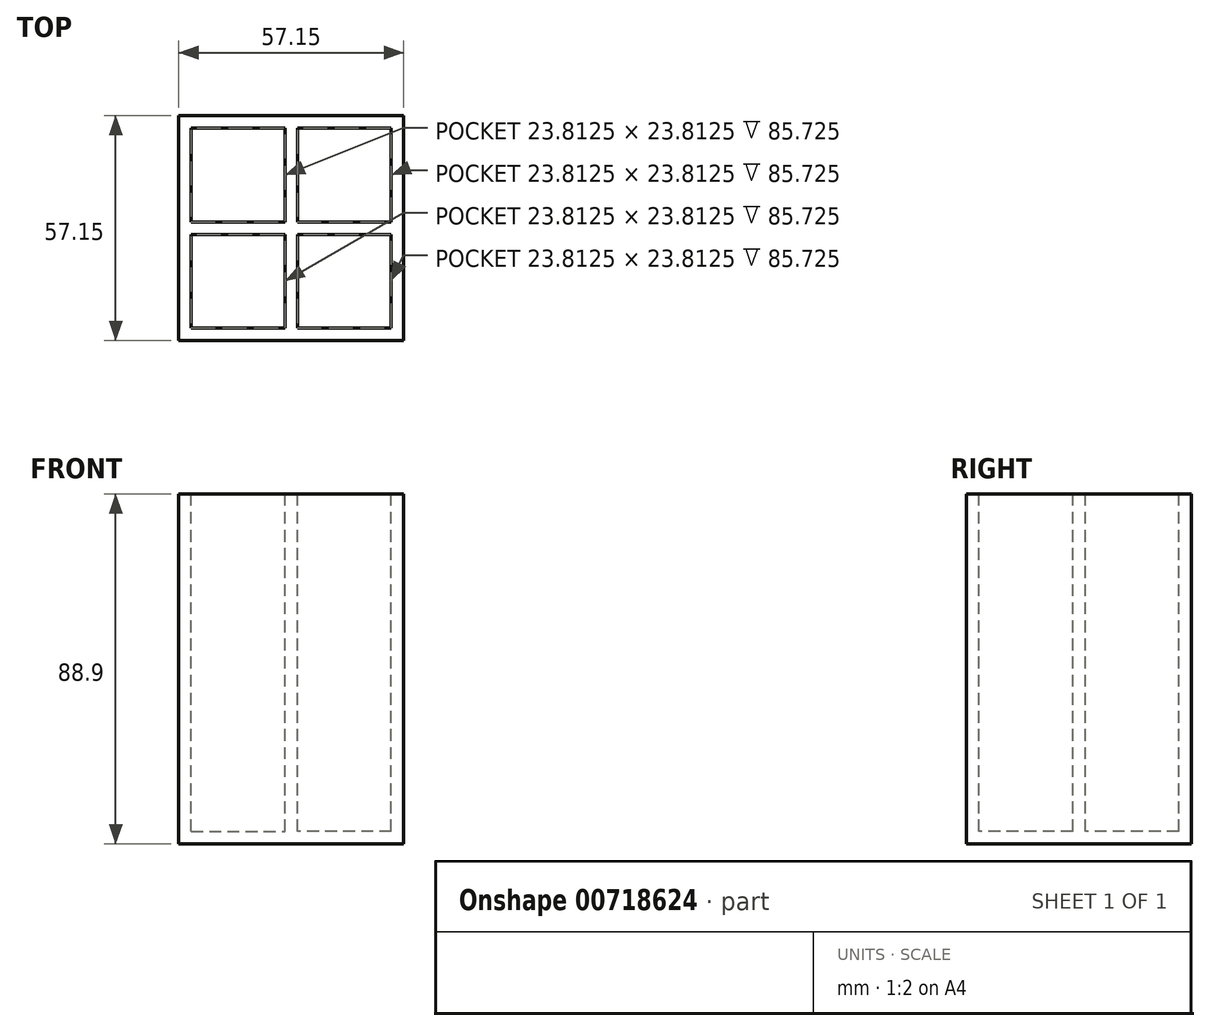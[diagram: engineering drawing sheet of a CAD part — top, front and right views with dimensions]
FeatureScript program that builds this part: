
annotation { "Feature Type Name" : "Feature", "Feature Type Description" : "" }
export const myFeature = defineFeature(function(context is Context, id is Id, definition is map)
    precondition{}
    {
        {
            var Q0;
            Q0=qCreatedBy(makeId("Front.planeOp"),FACE);
            var sketch = newSketch(context, id + "F0", { "sketchPlane" : qUnion([Q0])});
            skLineSegment(sketch, "E0.bottom", {"start": v(-30.53, 57.64) * mm, "end": v(26.62, 57.64) * mm});
            skLineSegment(sketch, "E0.top", {"start": v(-30.53, -31.26) * mm, "end": v(26.62, -31.26) * mm});
            skLineSegment(sketch, "E0.left", {"start": v(-30.53, 57.64) * mm, "end": v(-30.53, -31.26) * mm});
            skLineSegment(sketch, "E0.right", {"start": v(26.62, 57.64) * mm, "end": v(26.62, -31.26) * mm});
            skSolve(sketch);
        }
        {
            var Q0;
            Q0=qSketchRegion(id+"F0",true);
            extrude(context, id + "F1", {"entities" : qUnion([Q0]), "depth" : 57.15 * mm});
        }
        {
            var Q0;
            Q0=makeQuery(id+"F1.opExtrude","SWEPT_FACE",FACE,{"disambiguationData":[OSD([sQuery(id+"F0.wireOp",EDGE,"E0.bottom")])]});
            var sketch = newSketch(context, id + "F2", { "sketchPlane" : qUnion([Q0])});
            skLineSegment(sketch, "E1.bottom", {"start": v(-27.36, -3.18) * mm, "end": v(-3.54, -3.18) * mm});
            skLineSegment(sketch, "E1.top", {"start": v(-27.36, -26.99) * mm, "end": v(-3.54, -26.99) * mm});
            skLineSegment(sketch, "E1.left", {"start": v(-27.36, -3.18) * mm, "end": v(-27.36, -26.99) * mm});
            skLineSegment(sketch, "E1.right", {"start": v(-3.54, -3.17) * mm, "end": v(-3.54, -26.99) * mm});
            skSolve(sketch);
        }
        {
            var Q0;
            Q0=qSketchRegion(id+"F2",true);
            extrude(context, id + "F3", {"entities" : qUnion([Q0]), "operationType" : NewBodyOperationType.REMOVE, "oppositeDirection" : true, "depth" : 85.72 * mm});
        }
        {
            var Q0;
            Q0=makeQuery(id+"F1.opExtrude","SWEPT_FACE",FACE,{"disambiguationData":[OSD([sQuery(id+"F0.wireOp",EDGE,"E0.bottom")])]});
            var sketch = newSketch(context, id + "F4", { "sketchPlane" : qUnion([Q0])});
            skLineSegment(sketch, "E2.bottom", {"start": v(23.44, -3.17) * mm, "end": v(-0.37, -3.18) * mm});
            skLineSegment(sketch, "E2.top", {"start": v(23.44, -26.99) * mm, "end": v(-0.37, -26.99) * mm});
            skLineSegment(sketch, "E2.left", {"start": v(23.44, -3.17) * mm, "end": v(23.44, -26.99) * mm});
            skLineSegment(sketch, "E2.right", {"start": v(-0.37, -3.18) * mm, "end": v(-0.37, -26.99) * mm});
            skSolve(sketch);
        }
        {
            var Q0;
            Q0=qSketchRegion(id+"F4",true);
            extrude(context, id + "F5", {"entities" : qUnion([Q0]), "operationType" : NewBodyOperationType.REMOVE, "oppositeDirection" : true, "depth" : 85.72 * mm});
        }
        {
            var Q0;
            Q0=makeQuery(id+"F1.opExtrude","SWEPT_FACE",FACE,{"disambiguationData":[OSD([sQuery(id+"F0.wireOp",EDGE,"E0.bottom")])]});
            var sketch = newSketch(context, id + "F6", { "sketchPlane" : qUnion([Q0])});
            skLineSegment(sketch, "E3.bottom", {"start": v(-27.36, -30.16) * mm, "end": v(-3.54, -30.16) * mm});
            skLineSegment(sketch, "E3.top", {"start": v(-27.36, -53.98) * mm, "end": v(-3.54, -53.98) * mm});
            skLineSegment(sketch, "E3.left", {"start": v(-27.36, -30.16) * mm, "end": v(-27.36, -53.98) * mm});
            skLineSegment(sketch, "E3.right", {"start": v(-3.54, -30.16) * mm, "end": v(-3.54, -53.98) * mm});
            skSolve(sketch);
        }
        {
            var Q0;
            Q0=qSketchRegion(id+"F6",true);
            extrude(context, id + "F7", {"entities" : qUnion([Q0]), "operationType" : NewBodyOperationType.REMOVE, "oppositeDirection" : true, "depth" : 85.72 * mm});
        }
        {
            var Q0;
            Q0=makeQuery(id+"F1.opExtrude","SWEPT_FACE",FACE,{"disambiguationData":[OSD([sQuery(id+"F0.wireOp",EDGE,"E0.bottom")])]});
            var sketch = newSketch(context, id + "F8", { "sketchPlane" : qUnion([Q0])});
            skLineSegment(sketch, "E4.bottom", {"start": v(-0.37, -30.16) * mm, "end": v(23.44, -30.16) * mm});
            skLineSegment(sketch, "E4.top", {"start": v(-0.37, -53.98) * mm, "end": v(23.44, -53.98) * mm});
            skLineSegment(sketch, "E4.left", {"start": v(-0.37, -30.16) * mm, "end": v(-0.37, -53.98) * mm});
            skLineSegment(sketch, "E4.right", {"start": v(23.44, -30.16) * mm, "end": v(23.44, -53.98) * mm});
            skSolve(sketch);
        }
        {
            var Q0;
            Q0=qSketchRegion(id+"F8",true);
            extrude(context, id + "F9", {"entities" : qUnion([Q0]), "operationType" : NewBodyOperationType.REMOVE, "oppositeDirection" : true, "depth" : 85.72 * mm});
        }
    });
